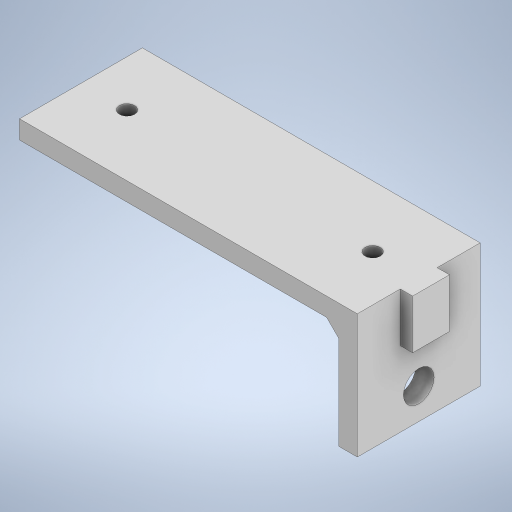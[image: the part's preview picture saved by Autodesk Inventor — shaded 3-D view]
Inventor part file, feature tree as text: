
AUTODESK INVENTOR PART (.ipt)
format: ipt  version: 2024 (Build 280153000, 153)  size: 257,536 bytes
history: native  units: mm
features: extrude x4, sketch x3, other x1, chamfer x1, projected_geometry x1
ambient origin geometry x8: Origin, YZ Plane, XZ Plane, XY Plane, X Axis, Y Axis, Z Axis, Center Point
bodies: Body1 (feature_tree)
feature tree (10):
  other  "솔리드1"
  sketch  "스케치1"
  extrude  "돌출1"  Depth=55.0mm
  extrude  "돌출2"  Depth=20.0mm
  sketch  "스케치2"
  chamfer  "모따기1"  Distance=3.0mm
  extrude  "돌출3"  Depth=3.0mm
  extrude  "돌출4"  Depth=17.2mm TaperAngle=0.0deg
  projected_geometry  "투영된 루프1"
  sketch  "스케치3"
